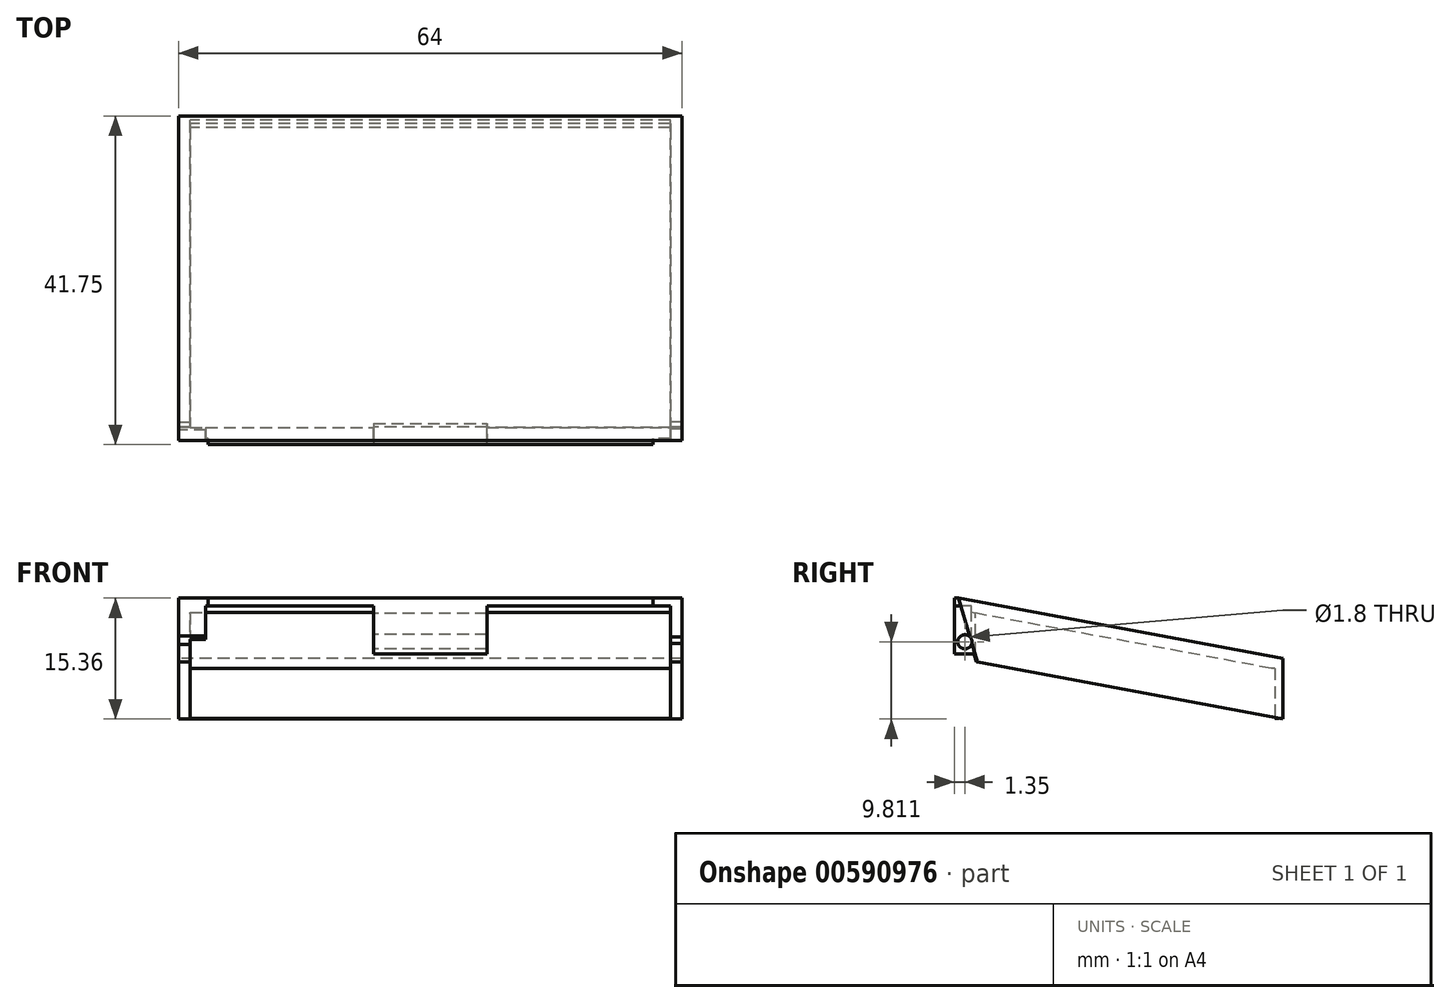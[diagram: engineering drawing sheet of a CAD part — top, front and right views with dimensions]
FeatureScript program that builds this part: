
annotation { "Feature Type Name" : "Feature", "Feature Type Description" : "" }
export const myFeature = defineFeature(function(context is Context, id is Id, definition is map)
    precondition{}
    {
        {
            var Q0;
            Q0=qCreatedBy(makeId("Right.planeOp"),FACE);
            var sketch = newSketch(context, id + "F0", { "sketchPlane" : qUnion([Q0])});
            skLineSegment(sketch, "E0", {"start": v(16.15, 0) * mm, "end": v(-25.1, 7.68) * mm});
            skLineSegment(sketch, "E1", {"start": v(-25.1, 7.68) * mm, "end": v(-25.1, 0) * mm});
            skLineSegment(sketch, "E2", {"start": v(16.15, 0) * mm, "end": v(16.15, -7.68) * mm});
            skLineSegment(sketch, "E3", {"start": v(-25.1, 0) * mm, "end": v(16.15, -7.68) * mm});
            skSolve(sketch);
        }
        {
            var Q0;
            Q0 = qSketchRegion(id + "F0", true);
            extrude(context, id + "F1", {"entities" : qUnion([Q0]), "depth" : 60 * mm, "offsetDistance" : 25 * mm});
        }
        {
            var Q0;
            Q0=makeQuery(id+"F1.opExtrude","SWEPT_FACE",FACE,{"disambiguationData":[OSD([sQuery(id+"F0.wireOp",EDGE,"E3")])]});
            shell(context, id + "F2", {"entities" : qUnion([Q0]), "thickness" : 1.5 * mm});
        }
        {
            var Q0;
            Q0=makeQuery(id+"F1.opExtrude","SWEPT_FACE",FACE,{"disambiguationData":[OSD([sQuery(id+"F0.wireOp",EDGE,"E1")])]});
            var sketch = newSketch(context, id + "F3", { "sketchPlane" : qUnion([Q0])});
            skLineSegment(sketch, "E4", {"start": v(37.3, 0) * mm, "end": v(30, 0) * mm});
            skLineSegment(sketch, "E5", {"start": v(30, 0) * mm, "end": v(22.7, 0) * mm});
            skLineSegment(sketch, "E6.bottom", {"start": v(1.49, 0) * mm, "end": v(58.51, 0) * mm});
            skLineSegment(sketch, "E6.top", {"start": v(1.49, 6.69) * mm, "end": v(58.51, 6.69) * mm});
            skLineSegment(sketch, "E6.left", {"start": v(1.49, 0) * mm, "end": v(1.49, 6.69) * mm});
            skLineSegment(sketch, "E6.right", {"start": v(58.51, 0) * mm, "end": v(58.51, 6.69) * mm});
            skSolve(sketch);
        }
        {
            var Q0;
            Q0 = qSketchRegion(id + "F3", true);
            extrude(context, id + "F4", {"entities" : qUnion([Q0]), "operationType" : NewBodyOperationType.REMOVE, "oppositeDirection" : true, "depth" : 1.7 * mm, "offsetDistance" : 25 * mm});
        }
        {
            var Q0;
            Q0=makeQuery(id+"F1.opExtrude","SWEPT_FACE",FACE,{"disambiguationData":[OSD([sQuery(id+"F0.wireOp",EDGE,"E3")])]});
            var sketch = newSketch(context, id + "F5", { "sketchPlane" : qUnion([Q0])});
            skLineSegment(sketch, "E7", {"start": v(58.5, 23.15) * mm, "end": v(58.51, 24.68) * mm});
            skLineSegment(sketch, "E8", {"start": v(58.51, 24.68) * mm, "end": v(1.49, 24.68) * mm});
            skLineSegment(sketch, "E9", {"start": v(1.49, 24.68) * mm, "end": v(1.5, 23.15) * mm});
            skLineSegment(sketch, "E10", {"start": v(1.5, 23.15) * mm, "end": v(58.5, 23.15) * mm});
            skSolve(sketch);
        }
        {
            var Q0;
            Q0 = qSketchRegion(id + "F5", true);
            extrude(context, id + "F6", {"entities" : qUnion([Q0]), "operationType" : NewBodyOperationType.REMOVE, "oppositeDirection" : true, "depth" : 1.5 * mm, "offsetDistance" : 25 * mm});
        }
        {
            var Q0;
            Q0=makeQuery(id+"F4.boolean.opBoolean","COPY",FACE,{"derivedFrom":makeQuery(id+"F4.opExtrude","SWEPT_FACE",FACE,{"disambiguationData":[OSD([sQuery(id+"F3.wireOp",EDGE,"E6.top")])]})});
            var sketch = newSketch(context, id + "F7", { "sketchPlane" : qUnion([Q0])});
            skLineSegment(sketch, "E11", {"start": v(30, 23.4) * mm, "end": v(37.2, 23.4) * mm});
            skLineSegment(sketch, "E12", {"start": v(30, 23.4) * mm, "end": v(22.8, 23.4) * mm});
            skLineSegment(sketch, "E13", {"start": v(22.8, 23.4) * mm, "end": v(22.8, 25.1) * mm});
            skLineSegment(sketch, "E14", {"start": v(22.8, 25.1) * mm, "end": v(37.2, 25.1) * mm});
            skLineSegment(sketch, "E15", {"start": v(37.2, 25.1) * mm, "end": v(37.2, 23.4) * mm});
            skSolve(sketch);
        }
        {
            var Q0;
            Q0 = qSketchRegion(id + "F7", true);
            extrude(context, id + "F8", {"entities" : qUnion([Q0]), "operationType" : NewBodyOperationType.ADD, "depth" : 7.7 * mm, "offsetDistance" : 25 * mm});
        }
        {
            var Q0;
            Q0=makeQuery(id+"F8.boolean.opBoolean","MERGE",FACE,{"derivedFrom":[makeQuery(id+"F1.opExtrude","SWEPT_FACE",FACE,{"disambiguationData":[OSD([sQuery(id+"F0.wireOp",EDGE,"E1")])]}),makeQuery(id+"F8.opExtrude","SWEPT_FACE",FACE,{"disambiguationData":[OSD([sQuery(id+"F7.wireOp",EDGE,"E14")])]})]});
            extrude(context, id + "F9", {"entities" : qUnion([Q0]), "operationType" : NewBodyOperationType.ADD, "depth" : 0.1 * mm, "offsetDistance" : 25 * mm});
        }
        {
            var Q0;
            Q0=makeQuery(id+"F9.opExtrude","CAP_FACE",FACE,{"disambiguationData":[OSD([sQuery(id+"F0.wireOp",EDGE,"E1"),sQuery(id+"F7.wireOp",EDGE,"E14")])],"isStart":false});
            extrude(context, id + "F10", {"entities" : qUnion([Q0]), "operationType" : NewBodyOperationType.ADD, "depth" : 0.4 * mm, "offsetDistance" : 25 * mm});
        }
        {
            var Q0;
            Q0=makeQuery(id+"F8.opExtrude","SWEPT_FACE",FACE,{"disambiguationData":[OSD([sQuery(id+"F7.wireOp",EDGE,"E11"),sQuery(id+"F7.wireOp",EDGE,"E12")])]});
            extrude(context, id + "F11", {"entities" : qUnion([Q0]), "operationType" : NewBodyOperationType.ADD, "depth" : 0.5 * mm, "offsetDistance" : 25 * mm});
        }
        {
            var Q0;
            {var subQ0=sQuery(id+"F7.wireOp",EDGE,"E13");var subQ1=sQuery(id+"F3.wireOp",EDGE,"E6.top");var subQ2=sQuery(id+"F7.wireOp",EDGE,"E14");Q0=makeQuery(id+"F11.boolean.opBoolean","MERGE",FACE,{"derivedFrom":[makeQuery(id+"F10.boolean.opBoolean","MERGE",FACE,{"derivedFrom":[makeQuery(id+"F9.boolean.opBoolean","MERGE",FACE,{"derivedFrom":[makeQuery(id+"F8.opExtrude","SWEPT_FACE",FACE,{"disambiguationData":[OSD([subQ0])]}),makeQuery(id+"F9.opExtrude","SWEPT_FACE",FACE,{"disambiguationData":[OSD([subQ1,subQ0,subQ2])]})]}),makeQuery(id+"F10.opExtrude","SWEPT_FACE",FACE,{"disambiguationData":[OSD([subQ1,subQ0,subQ2])]})]}),makeQuery(id+"F11.opExtrude","SWEPT_FACE",FACE,{"disambiguationData":[OSD([subQ1,sQuery(id+"F7.wireOp",EDGE,"E12"),subQ0])]})]});}
            var sketch = newSketch(context, id + "F12", { "sketchPlane" : qUnion([Q0])});
            skSolve(sketch);
        }
        {
            var Q0;
            {var subQ0=sQuery(id+"F7.wireOp",EDGE,"E13");var subQ2=sQuery(id+"F3.wireOp",EDGE,"E6.top");var subQ3=sQuery(id+"F7.wireOp",EDGE,"E14");Q0=makeQuery(id+"F12.imprint","IMPRINT",FACE,{"disambiguationData":[TD([[makeQuery(id+"F12.imprint","IMPRINT",EDGE,{"derivedFrom":makeQuery(id+"F10.opExtrude","CAP_EDGE",EDGE,{"disambiguationData":[OSD([subQ2,subQ0,subQ3])],"isStart":false})}),1.0]])]});}
            var sketch = newSketch(context, id + "F13", { "sketchPlane" : qUnion([Q0])});
            skCircle(sketch, "E16", {"center": v(24.25, 2.13) * mm, "radius": 0.9 * mm});
            skSolve(sketch);
        }
        {
            var Q0;
            Q0 = qSketchRegion(id + "F13", true);
            extrude(context, id + "F14", {"entities" : qUnion([Q0]), "operationType" : NewBodyOperationType.ADD, "depth" : 25 * mm, "offsetDistance" : 25 * mm});
        }
        {
            var Q0;
            Q0=makeQuery(id+"F14.opExtrude","CAP_FACE",FACE,{"disambiguationData":[OSD([sQuery(id+"F13.wireOp",EDGE,"E16")])],"isStart":false});
            extrude(context, id + "F15", {"entities" : qUnion([Q0]), "operationType" : NewBodyOperationType.REMOVE, "oppositeDirection" : true, "depth" : 63.1 * mm, "offsetDistance" : 25 * mm});
        }
        {
            var Q0;
            {var subQ0=sQuery(id+"F0.wireOp",EDGE,"E1");var subQ1=makeQuery(id+"F1.opExtrude","CAP_EDGE",EDGE,{"disambiguationData":[OSD([subQ0])],"isStart":true});Q0=makeQuery(id+"F10.boolean.opBoolean","MERGE",FACE,{"derivedFrom":[makeQuery(id+"F9.boolean.opBoolean","MERGE",FACE,{"derivedFrom":[makeQuery(id+"F1.opExtrude","CAP_FACE",FACE,{"disambiguationData":[OSD([sQuery(id+"F0.wireOp",EDGE,"E0"),subQ0,sQuery(id+"F0.wireOp",EDGE,"E2"),sQuery(id+"F0.wireOp",EDGE,"E3")])],"isStart":true}),makeQuery(id+"F9.opExtrude","SWEPT_FACE",FACE,{"disambiguationData":[OSD([subQ0]),TDD([subQ1])]})]}),makeQuery(id+"F10.opExtrude","SWEPT_FACE",FACE,{"disambiguationData":[OSD([subQ0]),TDD([makeQuery(id+"F9.opExtrude","CAP_EDGE",EDGE,{"disambiguationData":[OSD([subQ0]),TDD([subQ1])],"isStart":false})])]})]});}
            var sketch = newSketch(context, id + "F16", { "sketchPlane" : qUnion([Q0])});
            skLineSegment(sketch, "E17", {"start": v(22.8, -0.43) * mm, "end": v(25.1, 7.68) * mm});
            skLineSegment(sketch, "E18", {"start": v(25.1, 7.68) * mm, "end": v(25.6, 7.68) * mm});
            skLineSegment(sketch, "E19", {"start": v(25.6, 7.68) * mm, "end": v(25.6, 0) * mm});
            skLineSegment(sketch, "E20", {"start": v(25.6, 0) * mm, "end": v(22.8, -0.43) * mm});
            skSolve(sketch);
        }
        {
            var Q0;
            Q0 = qSketchRegion(id + "F16", true);
            extrude(context, id + "F17", {"entities" : qUnion([Q0]), "operationType" : NewBodyOperationType.REMOVE, "oppositeDirection" : true, "depth" : 1.8 * mm, "offsetDistance" : 25 * mm});
        }
        {
            var Q0;
            {var subQ0=sQuery(id+"F0.wireOp",EDGE,"E1");var subQ1=makeQuery(id+"F1.opExtrude","CAP_EDGE",EDGE,{"disambiguationData":[OSD([subQ0])],"isStart":false});Q0=makeQuery(id+"F10.boolean.opBoolean","MERGE",FACE,{"derivedFrom":[makeQuery(id+"F9.boolean.opBoolean","MERGE",FACE,{"derivedFrom":[makeQuery(id+"F1.opExtrude","CAP_FACE",FACE,{"disambiguationData":[OSD([sQuery(id+"F0.wireOp",EDGE,"E0"),subQ0,sQuery(id+"F0.wireOp",EDGE,"E2"),sQuery(id+"F0.wireOp",EDGE,"E3")])],"isStart":false}),makeQuery(id+"F9.opExtrude","SWEPT_FACE",FACE,{"disambiguationData":[OSD([subQ0]),TDD([subQ1])]})]}),makeQuery(id+"F10.opExtrude","SWEPT_FACE",FACE,{"disambiguationData":[OSD([subQ0]),TDD([makeQuery(id+"F9.opExtrude","CAP_EDGE",EDGE,{"disambiguationData":[OSD([subQ0]),TDD([subQ1])],"isStart":false})])]})]});}
            var sketch = newSketch(context, id + "F18", { "sketchPlane" : qUnion([Q0])});
            skLineSegment(sketch, "E21", {"start": v(-25.1, 7.68) * mm, "end": v(-22.64, -0.46) * mm});
            skLineSegment(sketch, "E22", {"start": v(-22.64, -0.46) * mm, "end": v(-25.6, 0) * mm});
            skLineSegment(sketch, "E23", {"start": v(-25.6, 0) * mm, "end": v(-25.6, 7.68) * mm});
            skLineSegment(sketch, "E24", {"start": v(-25.6, 7.68) * mm, "end": v(-25.1, 7.68) * mm});
            skSolve(sketch);
        }
        {
            var Q0;
            Q0 = qSketchRegion(id + "F18", true);
            extrude(context, id + "F19", {"entities" : qUnion([Q0]), "operationType" : NewBodyOperationType.REMOVE, "oppositeDirection" : true, "depth" : 1.7 * mm, "offsetDistance" : 25 * mm});
        }
        {
            var Q0;
            {var subQ0=sQuery(id+"F7.wireOp",EDGE,"E12");var subQ1=sQuery(id+"F7.wireOp",EDGE,"E11");var subQ2=sQuery(id+"F7.wireOp",EDGE,"E14");Q0=makeQuery(id+"F11.boolean.opBoolean","MERGE",FACE,{"derivedFrom":[makeQuery(id+"F10.boolean.opBoolean","MERGE",FACE,{"derivedFrom":[makeQuery(id+"F9.boolean.opBoolean","MERGE",FACE,{"derivedFrom":[makeQuery(id+"F8.opExtrude","CAP_FACE",FACE,{"disambiguationData":[OSD([subQ1,subQ0,sQuery(id+"F7.wireOp",EDGE,"E13"),subQ2,sQuery(id+"F7.wireOp",EDGE,"E15")])],"isStart":false}),makeQuery(id+"F9.opExtrude","SWEPT_FACE",FACE,{"disambiguationData":[OSD([subQ2])]})]}),makeQuery(id+"F10.opExtrude","SWEPT_FACE",FACE,{"disambiguationData":[OSD([subQ2])]})]}),makeQuery(id+"F11.opExtrude","SWEPT_FACE",FACE,{"disambiguationData":[OSD([subQ1,subQ0])]})]});}
            extrude(context, id + "F20", {"entities" : qUnion([Q0]), "operationType" : NewBodyOperationType.REMOVE, "oppositeDirection" : true, "depth" : 1.6 * mm, "offsetDistance" : 25 * mm});
        }
        {
            var Q0;
            {var subQ0=sQuery(id+"F0.wireOp",EDGE,"E1");var subQ1=makeQuery(id+"F1.opExtrude","CAP_EDGE",EDGE,{"disambiguationData":[OSD([subQ0])],"isStart":true});Q0=makeQuery(id+"F10.boolean.opBoolean","MERGE",FACE,{"derivedFrom":[makeQuery(id+"F9.boolean.opBoolean","MERGE",FACE,{"derivedFrom":[makeQuery(id+"F1.opExtrude","CAP_FACE",FACE,{"disambiguationData":[OSD([sQuery(id+"F0.wireOp",EDGE,"E0"),subQ0,sQuery(id+"F0.wireOp",EDGE,"E2"),sQuery(id+"F0.wireOp",EDGE,"E3")])],"isStart":true}),makeQuery(id+"F9.opExtrude","SWEPT_FACE",FACE,{"disambiguationData":[OSD([subQ0]),TDD([subQ1])]})]}),makeQuery(id+"F10.opExtrude","SWEPT_FACE",FACE,{"disambiguationData":[OSD([subQ0]),TDD([makeQuery(id+"F9.opExtrude","CAP_EDGE",EDGE,{"disambiguationData":[OSD([subQ0]),TDD([subQ1])],"isStart":false})])]})]});}
            extrude(context, id + "F21", {"entities" : qUnion([Q0]), "operationType" : NewBodyOperationType.ADD, "depth" : 2 * mm, "offsetDistance" : 25 * mm});
        }
        {
            var Q0;
            {var subQ0=sQuery(id+"F0.wireOp",EDGE,"E3");var subQ1=sQuery(id+"F0.wireOp",EDGE,"E2");var subQ2=sQuery(id+"F0.wireOp",EDGE,"E1");var subQ3=sQuery(id+"F0.wireOp",EDGE,"E0");Q0=makeQuery(id+"F2.opShell","OFFSET_FACE",FACE,{"disambiguationData":[OSD([subQ3,subQ2,subQ1,subQ0]),TDD([makeQuery(id+"F1.opExtrude","CAP_FACE",FACE,{"disambiguationData":[OSD([subQ3,subQ2,subQ1,subQ0])],"isStart":true})])]});}
            var Q1;
            {var subQ0=sQuery(id+"F3.wireOp",EDGE,"E6.top");var subQ1=makeQuery(id+"F4.boolean.opBoolean","COPY",FACE,{"derivedFrom":makeQuery(id+"F4.opExtrude","SWEPT_FACE",FACE,{"disambiguationData":[OSD([subQ0])]})});var subQ2=sQuery(id+"F3.wireOp",EDGE,"E6.left");var subQ3=makeQuery(id+"F4.boolean.opBoolean","COPY",FACE,{"derivedFrom":makeQuery(id+"F4.opExtrude","SWEPT_FACE",FACE,{"disambiguationData":[OSD([subQ2])]})});var subQ5=makeQuery(id+"F8.boolean.opBoolean","SPLIT",EDGE,{"disambiguationData":[TD([subQ3])],"derivedFrom":makeQuery(id+"F4.boolean.opBoolean","COPY",EDGE,{"derivedFrom":makeQuery(id+"F4.opExtrude","CAP_EDGE",EDGE,{"disambiguationData":[OSD([subQ0])],"isStart":true})})});var subQ6=makeQuery(id+"F4.boolean.opBoolean","COPY",FACE,{"derivedFrom":makeQuery(id+"F4.opExtrude","CAP_FACE",FACE,{"disambiguationData":[OSD([sQuery(id+"F3.wireOp",EDGE,"E6.bottom"),subQ0,subQ2,sQuery(id+"F3.wireOp",EDGE,"E6.right")])],"isStart":false})});var subQ11=makeQuery(id+"F9.opExtrude","SWEPT_FACE",FACE,{"disambiguationData":[OSD([subQ2])]});var subQ13=makeQuery(id+"F10.opExtrude","SWEPT_FACE",FACE,{"disambiguationData":[OSD([subQ2])]});Q1=makeQuery(id+"F17.boolean.opBoolean","SPLIT",FACE,{"disambiguationData":[TD([subQ6,subQ1,makeQuery(id+"F9.opExtrude","SWEPT_FACE",FACE,{"disambiguationData":[OSD([subQ0]),TDD([subQ5])]}),makeQuery(id+"F10.opExtrude","SWEPT_FACE",FACE,{"disambiguationData":[OSD([subQ0]),TDD([makeQuery(id+"F9.opExtrude","CAP_EDGE",EDGE,{"disambiguationData":[OSD([subQ0]),TDD([subQ5])],"isStart":false})])]}),makeQuery(id+"F15.boolean.opBoolean","COPY",FACE,{"disambiguationData":[TD([subQ3])],"derivedFrom":makeQuery(id+"F15.opExtrude","SWEPT_FACE",FACE,{"disambiguationData":[OSD([sQuery(id+"F13.wireOp",EDGE,"E16")])]})}),makeQuery(id+"F17.opExtrude","SWEPT_FACE",FACE,{"disambiguationData":[OSD([sQuery(id+"F16.wireOp",EDGE,"E17")])]})])],"derivedFrom":makeQuery(id+"F10.boolean.opBoolean","MERGE",FACE,{"derivedFrom":[makeQuery(id+"F9.boolean.opBoolean","MERGE",FACE,{"derivedFrom":[subQ3,subQ11]}),subQ13]})});}
            extrude(context, id + "F22", {"entities" : qUnion([Q0, Q1]), "operationType" : NewBodyOperationType.REMOVE, "oppositeDirection" : true, "depth" : 2 * mm, "offsetDistance" : 25 * mm});
        }
        {
            var Q0;
            {var subQ0=sQuery(id+"F0.wireOp",EDGE,"E1");var subQ1=makeQuery(id+"F1.opExtrude","CAP_EDGE",EDGE,{"disambiguationData":[OSD([subQ0])],"isStart":false});Q0=makeQuery(id+"F10.boolean.opBoolean","MERGE",FACE,{"derivedFrom":[makeQuery(id+"F9.boolean.opBoolean","MERGE",FACE,{"derivedFrom":[makeQuery(id+"F1.opExtrude","CAP_FACE",FACE,{"disambiguationData":[OSD([sQuery(id+"F0.wireOp",EDGE,"E0"),subQ0,sQuery(id+"F0.wireOp",EDGE,"E2"),sQuery(id+"F0.wireOp",EDGE,"E3")])],"isStart":false}),makeQuery(id+"F9.opExtrude","SWEPT_FACE",FACE,{"disambiguationData":[OSD([subQ0]),TDD([subQ1])]})]}),makeQuery(id+"F10.opExtrude","SWEPT_FACE",FACE,{"disambiguationData":[OSD([subQ0]),TDD([makeQuery(id+"F9.opExtrude","CAP_EDGE",EDGE,{"disambiguationData":[OSD([subQ0]),TDD([subQ1])],"isStart":false})])]})]});}
            extrude(context, id + "F23", {"entities" : qUnion([Q0]), "operationType" : NewBodyOperationType.ADD, "depth" : 2 * mm, "offsetDistance" : 25 * mm});
        }
        {
            var Q0;
            {var subQ0=sQuery(id+"F3.wireOp",EDGE,"E6.right");Q0=makeQuery(id+"F10.boolean.opBoolean","MERGE",FACE,{"derivedFrom":[makeQuery(id+"F9.boolean.opBoolean","MERGE",FACE,{"derivedFrom":[makeQuery(id+"F4.boolean.opBoolean","COPY",FACE,{"derivedFrom":makeQuery(id+"F4.opExtrude","SWEPT_FACE",FACE,{"disambiguationData":[OSD([subQ0])]})}),makeQuery(id+"F9.opExtrude","SWEPT_FACE",FACE,{"disambiguationData":[OSD([subQ0])]})]}),makeQuery(id+"F10.opExtrude","SWEPT_FACE",FACE,{"disambiguationData":[OSD([subQ0])]})]});}
            var Q1;
            {var subQ0=sQuery(id+"F0.wireOp",EDGE,"E3");var subQ1=sQuery(id+"F0.wireOp",EDGE,"E2");var subQ2=sQuery(id+"F0.wireOp",EDGE,"E1");var subQ3=sQuery(id+"F0.wireOp",EDGE,"E0");Q1=makeQuery(id+"F2.opShell","OFFSET_FACE",FACE,{"disambiguationData":[OSD([subQ3,subQ2,subQ1,subQ0]),TDD([makeQuery(id+"F1.opExtrude","CAP_FACE",FACE,{"disambiguationData":[OSD([subQ3,subQ2,subQ1,subQ0])],"isStart":false})])]});}
            extrude(context, id + "F24", {"entities" : qUnion([Q0, Q1]), "operationType" : NewBodyOperationType.REMOVE, "oppositeDirection" : true, "depth" : 2 * mm, "offsetDistance" : 25 * mm});
        }
        {
            var Q0;
            {var subQ0=sQuery(id+"F0.wireOp",EDGE,"E2");Q0=makeQuery(id+"F24.boolean.opBoolean","MERGE",FACE,{"derivedFrom":[makeQuery(id+"F22.boolean.opBoolean","MERGE",FACE,{"derivedFrom":[makeQuery(id+"F2.opShell","OFFSET_FACE",FACE,{"disambiguationData":[OSD([subQ0])]}),makeQuery(id+"F22.opExtrude","SWEPT_FACE",FACE,{"disambiguationData":[OSD([subQ0])]})]}),makeQuery(id+"F24.opExtrude","SWEPT_FACE",FACE,{"disambiguationData":[OSD([subQ0])]})]});}
            extrude(context, id + "F25", {"entities" : qUnion([Q0]), "operationType" : NewBodyOperationType.REMOVE, "oppositeDirection" : true, "depth" : 0.5 * mm, "offsetDistance" : 25 * mm});
        }
        {
            var Q0;
            Q0=makeQuery(id+"F25.boolean.opBoolean","COPY",FACE,{"derivedFrom":makeQuery(id+"F25.opExtrude","CAP_FACE",FACE,{"disambiguationData":[OSD([sQuery(id+"F0.wireOp",EDGE,"E2")])],"isStart":false})});
            extrude(context, id + "F26", {"entities" : qUnion([Q0]), "operationType" : NewBodyOperationType.REMOVE, "oppositeDirection" : true, "depth" : 0.5 * mm, "offsetDistance" : 25 * mm});
        }
        {
            var Q0;
            {var subQ0=sQuery(id+"F0.wireOp",EDGE,"E3");var subQ1=sQuery(id+"F0.wireOp",EDGE,"E2");Q0=makeQuery(id+"F26.boolean.opBoolean","MERGE",FACE,{"derivedFrom":[makeQuery(id+"F25.boolean.opBoolean","COPY",FACE,{"derivedFrom":makeQuery(id+"F25.opExtrude","SWEPT_FACE",FACE,{"disambiguationData":[OSD([subQ1,subQ0])]})}),makeQuery(id+"F26.opExtrude","SWEPT_FACE",FACE,{"disambiguationData":[OSD([subQ1,subQ0])]})]});}
            extrude(context, id + "F27", {"entities" : qUnion([Q0]), "operationType" : NewBodyOperationType.REMOVE, "oppositeDirection" : true, "depth" : 25 * mm, "offsetDistance" : 25 * mm});
        }
        {
            var Q0;
            {var subQ0=sQuery(id+"F0.wireOp",EDGE,"E3");var subQ1=sQuery(id+"F0.wireOp",EDGE,"E2");Q0=makeQuery(id+"F27.boolean.opBoolean","MERGE",FACE,{"derivedFrom":[makeQuery(id+"F26.boolean.opBoolean","COPY",FACE,{"derivedFrom":makeQuery(id+"F26.opExtrude","CAP_FACE",FACE,{"disambiguationData":[OSD([subQ1])],"isStart":false})}),makeQuery(id+"F27.opExtrude","SWEPT_FACE",FACE,{"disambiguationData":[OSD([subQ1,subQ0]),TDD([makeQuery(id+"F26.boolean.opBoolean","COPY",EDGE,{"derivedFrom":makeQuery(id+"F26.opExtrude","CAP_EDGE",EDGE,{"disambiguationData":[OSD([subQ1,subQ0])],"isStart":false})})])]})]});}
            extrude(context, id + "F28", {"entities" : qUnion([Q0]), "operationType" : NewBodyOperationType.ADD, "depth" : 0.5 * mm, "offsetDistance" : 25 * mm});
        }
    });
